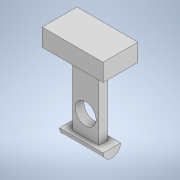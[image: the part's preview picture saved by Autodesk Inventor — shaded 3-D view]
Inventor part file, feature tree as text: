
AUTODESK INVENTOR PART (.ipt)
format: ipt  version: 2021 (Build 250183000, 183)  size: 147,456 bytes
history: native  units: mm
features: extrude x6, sketch x6
ambient origin geometry x8: Origin, YZ Plane, XZ Plane, XY Plane, X Axis, Y Axis, Z Axis, Center Point
bodies: Solid1 (feature_tree)
feature tree (12):
  extrude  "Extrusion1"  Depth=10.0mm
  extrude  "Extrusion2"  Depth=2.5mm
  extrude  "Extrusion3"  Depth=10.0mm
  extrude  "Extrusion4"  Depth=10.0mm TaperAngle=0.0deg
  extrude  "Extrusion5"  Depth=10.0mm
  extrude  "Extrusion6"  Depth=25.0mm
  sketch  "Sketch1"  dims[d0=40.0mm d1=10.0mm]
  sketch  "Sketch2"  dims[d2=5.0mm d3=2.5mm]
  sketch  "Sketch3"  dims[d4=20.0mm d5=10.0mm]
  sketch  "Sketch4"  dims[d6=15.0mm d7=0.0mm d8=10.0mm d9=0.0mm]
  sketch  "Sketch5"  dims[d10=10.0mm d11=0.0mm d12=12.0mm]
  sketch  "Sketch6"  dims[d13=5.0mm d14=0.0mm d15=25.0mm d16=10.0mm d17=10.0mm d18=0.0mm d19=5.0mm d20=25.0mm d21=0.0mm]
